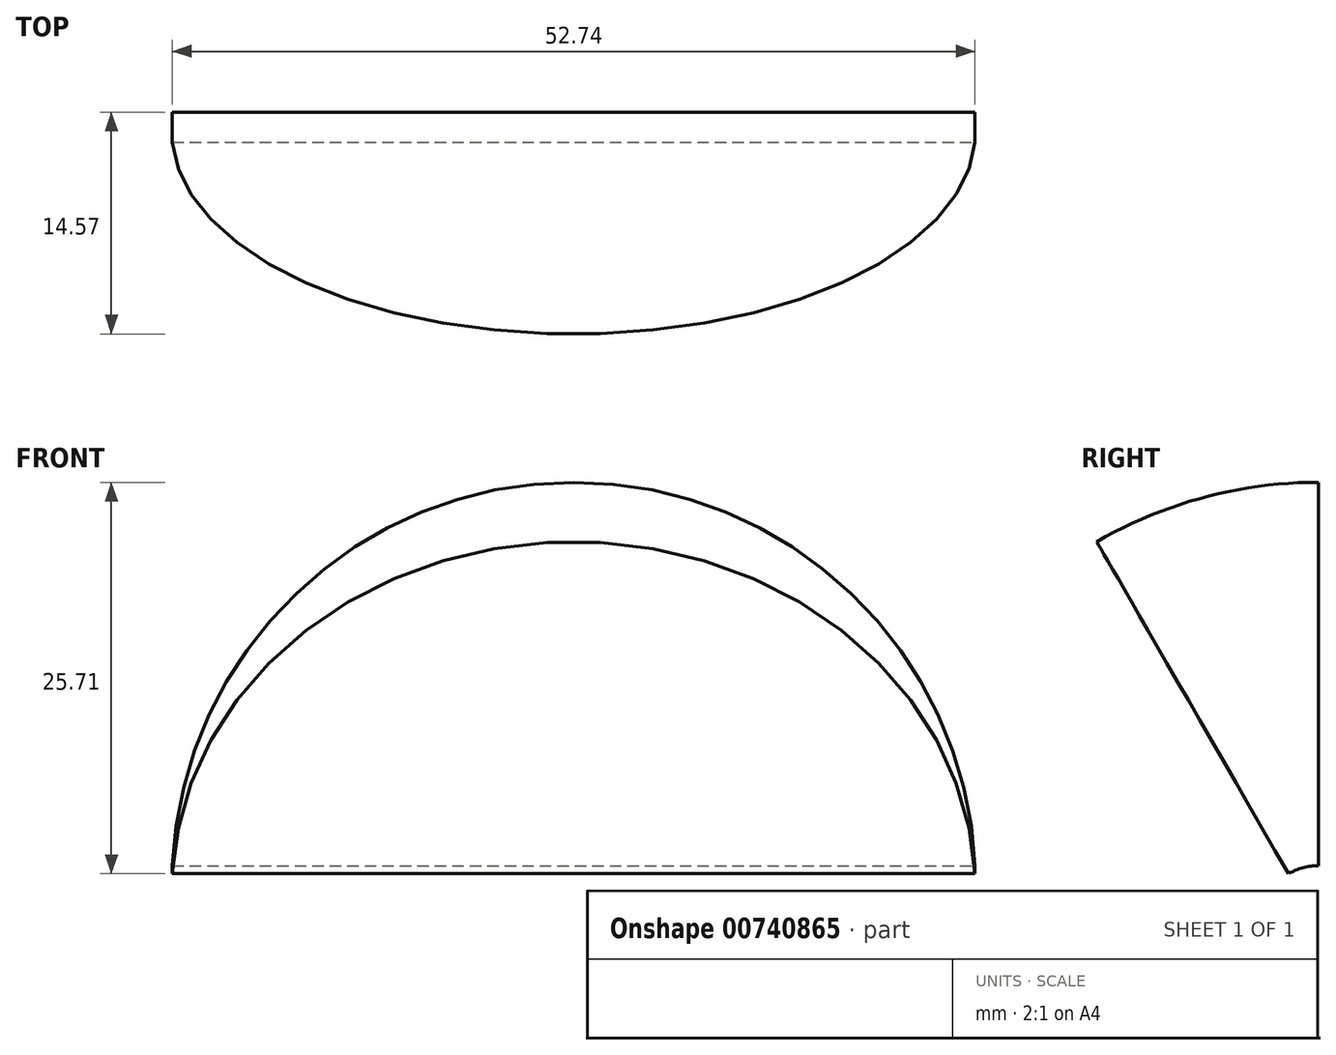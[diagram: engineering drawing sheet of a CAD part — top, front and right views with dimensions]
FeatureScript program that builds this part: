
annotation { "Feature Type Name" : "Feature", "Feature Type Description" : "" }
export const myFeature = defineFeature(function(context is Context, id is Id, definition is map)
    precondition{}
    {
        {
            var Q0;
            Q0=qCreatedBy(makeId("Front.planeOp"),FACE);
            var sketch = newSketch(context, id + "F0", { "sketchPlane" : qUnion([Q0])});
            skArc(sketch, "E0", {"start": v(26.52, 0) * mm, "mid": v(0.15, 25.18) * mm, "end": v(-26.22, 0) * mm});
            skLineSegment(sketch, "E1", {"start": v(-26.22, 0) * mm, "end": v(26.52, 0) * mm});
            skSolve(sketch);
        }
        {
            var Q0;
            Q0=qCreatedBy(makeId("Front.planeOp"),FACE);
            var sketch = newSketch(context, id + "F1", { "sketchPlane" : qUnion([Q0])});
            skLineSegment(sketch, "E2", {"start": v(-25.05, -3.96) * mm, "end": v(18.66, -3.96) * mm});
            skSolve(sketch);
        }
        {
            var Q0;
            Q0=makeQuery(id+"F0.imprint","IMPRINT",FACE,{"disambiguationData":[TD([[makeQuery(id+"F0.imprint","IMPRINT",EDGE,{"derivedFrom":sQuery(id+"F0.wireOp",EDGE,"E0")}),1.0]])]});
            var Q1;
            Q1=sQuery(id+"F1.wireOp",EDGE,"E2");
            revolve(context, id + "F2", {"surfaceOperationType" : NewSurfaceOperationType.NEW, "entities" : qUnion([Q0]), "axis" : qUnion([Q1]), "revolveType" : RevolveType.ONE_DIRECTION, "angle" : 30 * degree});
        }
    });
